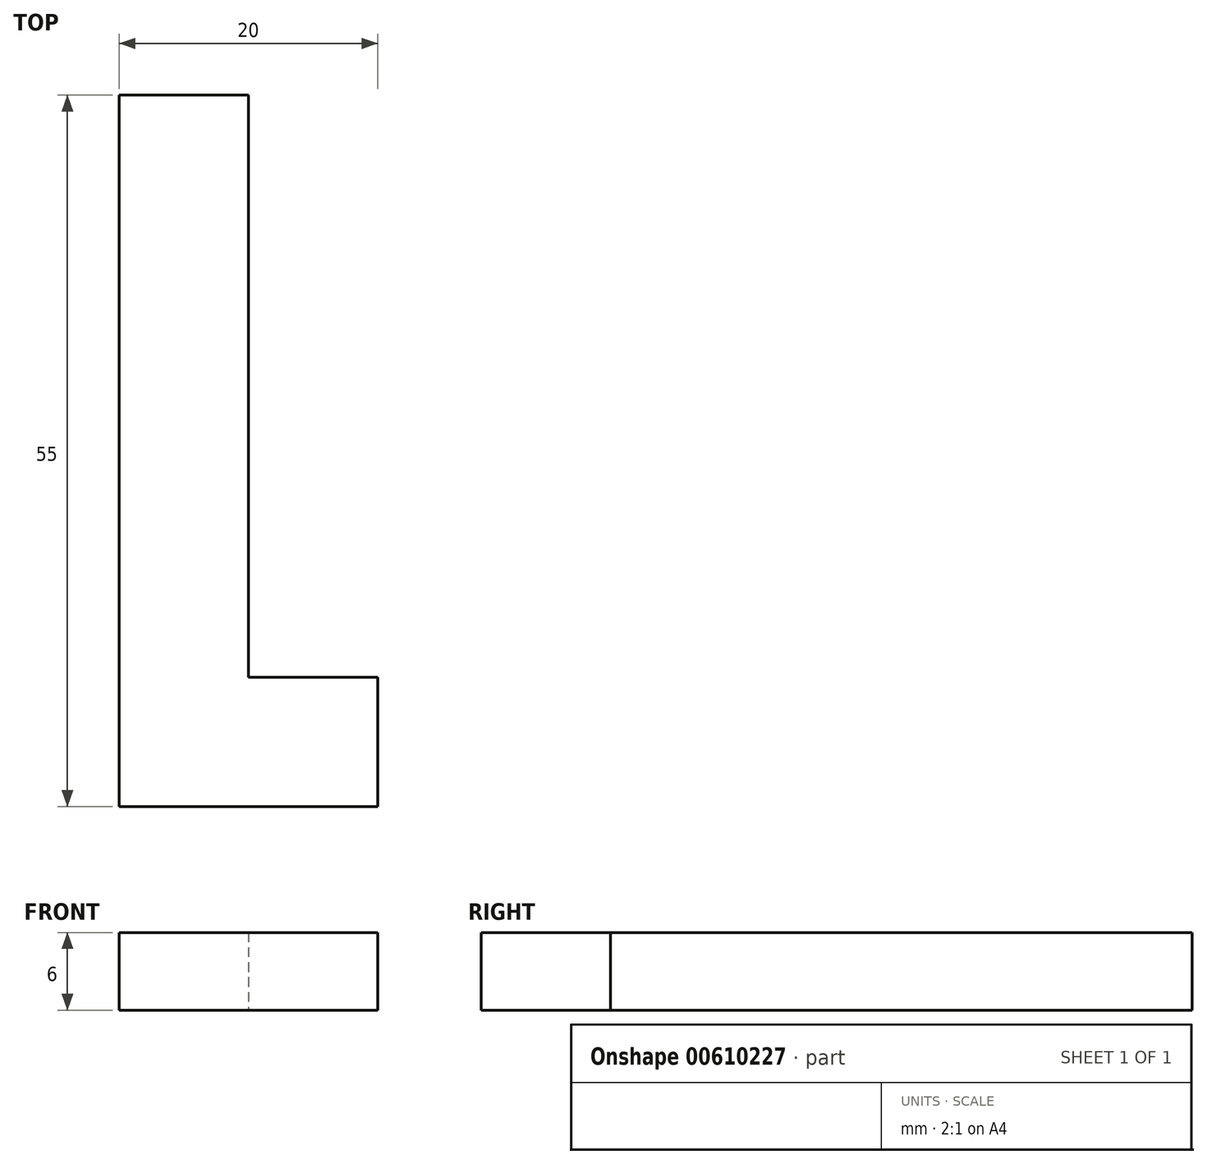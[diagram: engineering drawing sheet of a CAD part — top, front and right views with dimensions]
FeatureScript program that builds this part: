
annotation { "Feature Type Name" : "Feature", "Feature Type Description" : "" }
export const myFeature = defineFeature(function(context is Context, id is Id, definition is map)
    precondition{}
    {
        {
            var Q0;
            Q0=qCreatedBy(makeId("Top.planeOp"),FACE);
            var sketch = newSketch(context, id + "F0", { "sketchPlane" : qUnion([Q0])});
            skLineSegment(sketch, "E0.bottom", {"start": v(-12.73, 24.34) * mm, "end": v(-2.73, 24.34) * mm});
            skLineSegment(sketch, "E1.bottom", {"start": v(-12.73, -30.66) * mm, "end": v(7.27, -30.66) * mm});
            skLineSegment(sketch, "E2", {"start": v(-12.73, 24.34) * mm, "end": v(-12.73, -30.66) * mm});
            skLineSegment(sketch, "E3", {"start": v(-2.73, 24.34) * mm, "end": v(-2.73, -20.66) * mm});
            skLineSegment(sketch, "E4", {"start": v(-2.73, -20.66) * mm, "end": v(7.27, -20.66) * mm});
            skLineSegment(sketch, "E5", {"start": v(7.27, -20.66) * mm, "end": v(7.27, -30.66) * mm});
            skSolve(sketch);
        }
        {
            var Q0;
            Q0 = qSketchRegion(id + "F0", true);
            extrude(context, id + "F1", {"entities" : qUnion([Q0]), "depth" : 6 * mm, "offsetDistance" : 25 * mm});
        }
    });
